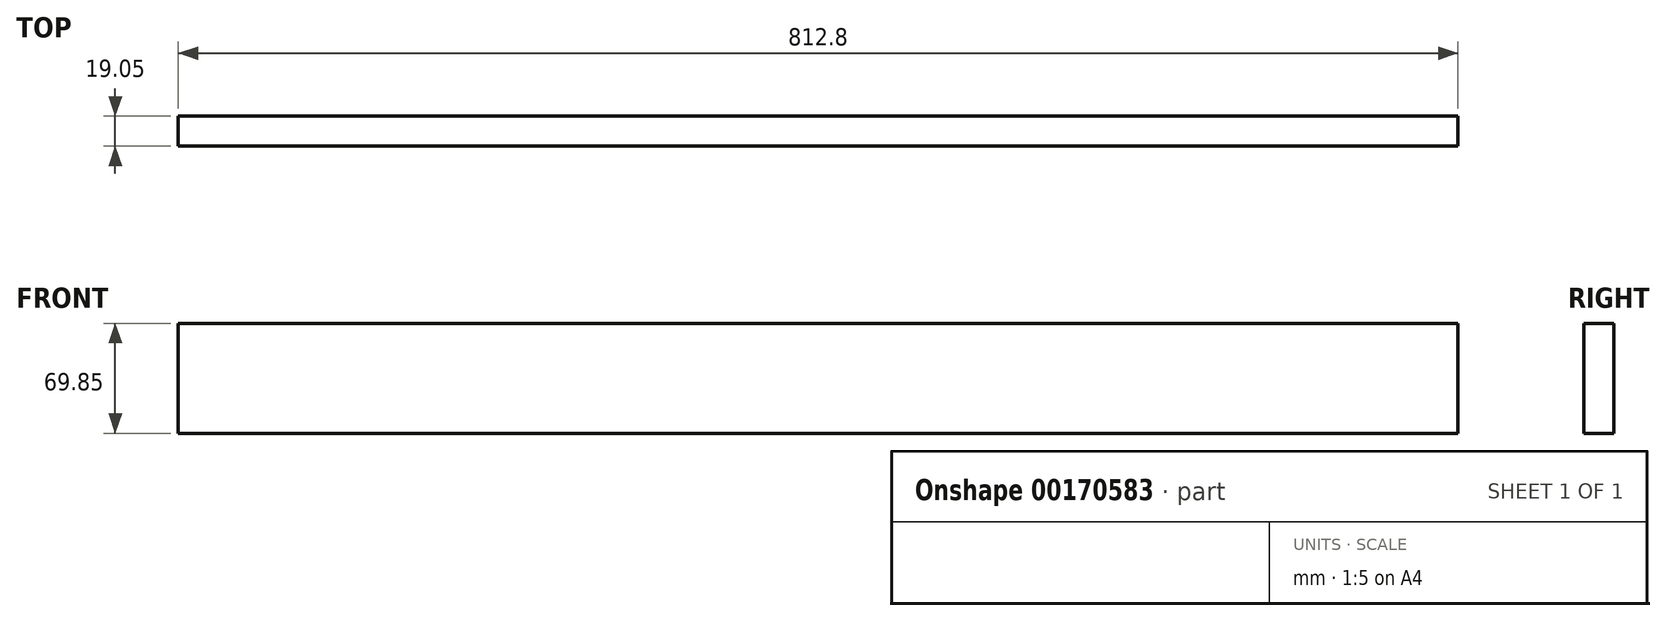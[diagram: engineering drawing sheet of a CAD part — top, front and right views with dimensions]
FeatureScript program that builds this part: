
annotation { "Feature Type Name" : "Feature", "Feature Type Description" : "" }
export const myFeature = defineFeature(function(context is Context, id is Id, definition is map)
    precondition{}
    {
        {
            var Q0;
            Q0=qCreatedBy(makeId("Right.planeOp"),FACE);
            var sketch = newSketch(context, id + "F0", { "sketchPlane" : qUnion([Q0])});
            skLineSegment(sketch, "E0.bottom", {"start": v(0, 0) * mm, "end": v(19.05, 0) * mm});
            skLineSegment(sketch, "E0.top", {"start": v(0, -69.85) * mm, "end": v(19.05, -69.85) * mm});
            skLineSegment(sketch, "E0.left", {"start": v(0, 0) * mm, "end": v(0, -69.85) * mm});
            skLineSegment(sketch, "E0.right", {"start": v(19.05, 0) * mm, "end": v(19.05, -69.85) * mm});
            skSolve(sketch);
        }
        {
            var Q0;
            Q0 = qSketchRegion(id + "F0", true);
            extrude(context, id + "F1", {"entities" : qUnion([Q0]), "endBound" : BoundingType.SYMMETRIC, "depth" : 812.8 * mm});
        }
    });
